# Revit family: Furniture_Table_Spacestor_Volute Boardroom Table
name_source: partatom
category: Furniture
revit_build: Autodesk Revit 2015 (Build: 20140223_1515(x64)
units: mm (PartAtom-declared; Revit-internal decimal feet)

## types (20) — shared parameters
Assembly Code = E2020200
Description = Volute Boardroom Barrel Shaped Table
Height = 755 mm  [stored 2.47703 ft]
Legs Finish = Spacestor Polished Steel
Manufacturer = Spacestor
Model = Volute
Table Top Finish = Spacestor White Table Top
URL = http://spacestor.uk.com

## per-type parameters (varying)
| type | Boat | Double D-End | Oval | Rectangular |
| double d-ended - 2000w x 1000d x 755h | No | Yes | No | No |
| boat-shaped - 2000w x 1000_800d x 755h | Yes | No | No | No |
| oval-shaped - 2000w x 1000d x 755h | No | No | Yes | No |
| rectangular - 2000w x 1000d x 755h | No | No | No | Yes |
| boat-shaped - 2400w x 1200_1000d x 755h | Yes | No | No | No |
| boat-shaped - 3000w x 1200_1000d x 755h | Yes | No | No | No |
| boat-shaped - 3600w x 1200_1000d x 755h | Yes | No | No | No |
| boat-shaped - 4800w x 1200_1000d x 755h | Yes | No | No | No |
| double d-ended - 2400w x 1200d x 755h | No | Yes | No | No |
| double d-ended - 3000w x 1200d x 755h | No | Yes | No | No |
| double d-ended - 3600w x 1200d x 755h | No | Yes | No | No |
| double d-ended - 4800w x 1200d x 755h | No | Yes | No | No |
| oval-shaped - 2400w x 1200d x 755h | No | No | Yes | No |
| oval-shaped - 3000w x 1200d x 755h | No | No | Yes | No |
| oval-shaped - 3600w x 1200d x 755h | No | No | Yes | No |
| oval-shaped - 4800w x 1200d x 755h | No | No | Yes | No |
| rectangular - 2400w x 1200d x 755h | No | No | No | Yes |
| rectangular - 3000w x 1200d x 755h | No | No | No | Yes |
| rectangular - 3600w x 1200d x 755h | No | No | No | Yes |
| rectangular - 4800w x 1200d x 755h | No | No | No | Yes |

note: [stored X ft] marks values corroborated as IEEE doubles in the binary element streams (Revit-internal decimal feet)

## geometry (parser evidence)
native form markers: Sweep x4
no freeform markers — native parametric forms only
